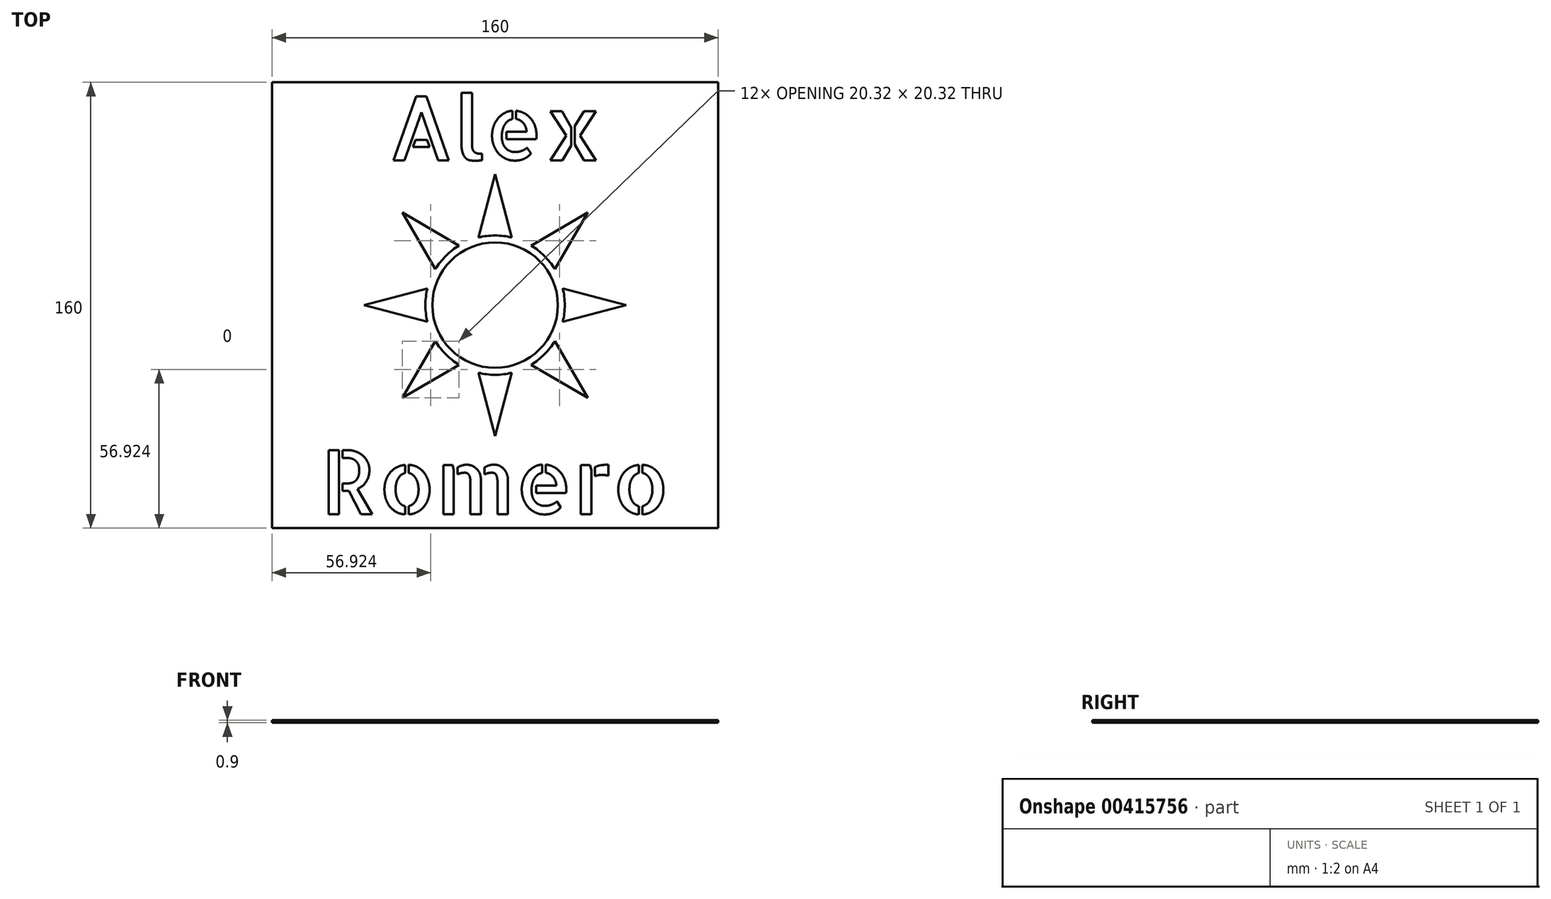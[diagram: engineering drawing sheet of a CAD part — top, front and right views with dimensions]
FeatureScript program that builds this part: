
annotation { "Feature Type Name" : "Feature", "Feature Type Description" : "" }
export const myFeature = defineFeature(function(context is Context, id is Id, definition is map)
    precondition{}
    {
        {
            var Q0;
            Q0=qCreatedBy(makeId("Top.planeOp"),FACE);
            var sketch = newSketch(context, id + "F0", { "sketchPlane" : qUnion([Q0])});
            skLineSegment(sketch, "E0.bottom", {"start": v(0, 0) * mm, "end": v(160, 0) * mm});
            skLineSegment(sketch, "E0.top", {"start": v(0, 160) * mm, "end": v(160, 160) * mm});
            skLineSegment(sketch, "E0.left", {"start": v(0, 0) * mm, "end": v(0, 160) * mm});
            skLineSegment(sketch, "E0.right", {"start": v(160, 0) * mm, "end": v(160, 160) * mm});
            skCircle(sketch, "E1", {"center": v(80, 80) * mm, "radius": 22.5 * mm});
            skLineSegment(sketch, "E2", {"start": v(0, 80) * mm, "end": v(160, 80) * mm, "construction": true});
            skLineSegment(sketch, "E3", {"start": v(80, 0) * mm, "end": v(80, 160) * mm, "construction": true});
            skText(sketch, "E4", { "text": "Alex", "fontName": "AllertaStencil-Regular.ttf"});
            skText(sketch, "E5", { "text": "Romero", "fontName": "AllertaStencil-Regular.ttf"});
            skArc(sketch, "E6", {"start": v(74, 104.27) * mm, "mid": v(80, 105) * mm, "end": v(86, 104.27) * mm});
            skLineSegment(sketch, "E7", {"start": v(74, 104.27) * mm, "end": v(80, 127) * mm});
            skLineSegment(sketch, "E8", {"start": v(80, 127) * mm, "end": v(86, 104.27) * mm});
            skLineSegment(sketch, "E9.1.0", {"start": v(92.92, 101.4) * mm, "end": v(113.23, 113.23) * mm});
            skLineSegment(sketch, "E9.1.1", {"start": v(113.23, 113.23) * mm, "end": v(101.4, 92.92) * mm});
            skArc(sketch, "E9.1.2", {"start": v(92.92, 101.4) * mm, "mid": v(97.68, 97.68) * mm, "end": v(101.4, 92.92) * mm});
            skLineSegment(sketch, "E9.2.0", {"start": v(104.27, 86) * mm, "end": v(127, 80) * mm});
            skLineSegment(sketch, "E9.2.1", {"start": v(127, 80) * mm, "end": v(104.27, 74) * mm});
            skArc(sketch, "E9.2.2", {"start": v(104.27, 86) * mm, "mid": v(105, 80) * mm, "end": v(104.27, 74) * mm});
            skLineSegment(sketch, "E9.3.0", {"start": v(101.4, 67.08) * mm, "end": v(113.23, 46.77) * mm});
            skLineSegment(sketch, "E9.3.1", {"start": v(113.23, 46.77) * mm, "end": v(92.92, 58.6) * mm});
            skArc(sketch, "E9.3.2", {"start": v(101.4, 67.08) * mm, "mid": v(97.68, 62.32) * mm, "end": v(92.92, 58.6) * mm});
            skLineSegment(sketch, "E9.anchor1", {"start": v(80, 80) * mm, "end": v(74, 104.27) * mm, "construction": true});
            skLineSegment(sketch, "E9.anchor2", {"start": v(80, 80) * mm, "end": v(58.6, 92.92) * mm, "construction": true});
            skLineSegment(sketch, "E10", {"start": v(80, 80) * mm, "end": v(33.62, 126.38) * mm, "construction": true});
            skLineSegment(sketch, "E11", {"start": v(80, 80) * mm, "end": v(42.08, 97.68) * mm, "construction": true});
            skLineSegment(sketch, "E12", {"start": v(80, 80) * mm, "end": v(62.27, 118.03) * mm, "construction": true});
            skLineSegment(sketch, "E13.anchor1", {"start": v(80, 80) * mm, "end": v(52.81, 92.68) * mm, "construction": true});
            skLineSegment(sketch, "E14.1.4.0", {"start": v(86, 55.73) * mm, "end": v(80, 33) * mm});
            skLineSegment(sketch, "E14.3.4.0", {"start": v(80, 33) * mm, "end": v(74, 55.73) * mm});
            skArc(sketch, "E14.6.4.0", {"start": v(86, 55.73) * mm, "mid": v(80, 55) * mm, "end": v(74, 55.73) * mm});
            skLineSegment(sketch, "E14.1.5.0", {"start": v(67.08, 58.6) * mm, "end": v(46.77, 46.77) * mm});
            skLineSegment(sketch, "E14.3.5.0", {"start": v(46.77, 46.77) * mm, "end": v(58.6, 67.08) * mm});
            skArc(sketch, "E14.6.5.0", {"start": v(67.08, 58.6) * mm, "mid": v(62.32, 62.32) * mm, "end": v(58.6, 67.08) * mm});
            skLineSegment(sketch, "E14.1.6.0", {"start": v(55.73, 74) * mm, "end": v(33, 80) * mm});
            skLineSegment(sketch, "E14.3.6.0", {"start": v(33, 80) * mm, "end": v(55.73, 86) * mm});
            skArc(sketch, "E14.6.6.0", {"start": v(55.73, 74) * mm, "mid": v(55, 80) * mm, "end": v(55.73, 86) * mm});
            skLineSegment(sketch, "E14.1.7.0", {"start": v(58.6, 92.92) * mm, "end": v(46.77, 113.23) * mm});
            skLineSegment(sketch, "E14.3.7.0", {"start": v(46.77, 113.23) * mm, "end": v(67.08, 101.4) * mm});
            skArc(sketch, "E14.6.7.0", {"start": v(58.6, 92.92) * mm, "mid": v(62.32, 97.68) * mm, "end": v(67.08, 101.4) * mm});
            const initialGuessF0  = {"E4": [0.04165, 0.132, 1, 0, 0.023], "E5": [0.01747, 0.005, 1, 0, 0.023]};
            skSetInitialGuess(sketch, initialGuessF0);
            skSolve(sketch);
        }
        {
            var Q0;
            Q0=makeQuery(id+"F0.imprint","IMPRINT",FACE,{"disambiguationData":[TD([[makeQuery(id+"F0.imprint","IMPRINT",EDGE,{"derivedFrom":sQuery(id+"F0.wireOp",EDGE,"E0.bottom")}),1.0]])]});
            extrude(context, id + "F1", {"entities" : qUnion([Q0]), "depth" : 0.9 * mm});
        }
    });
